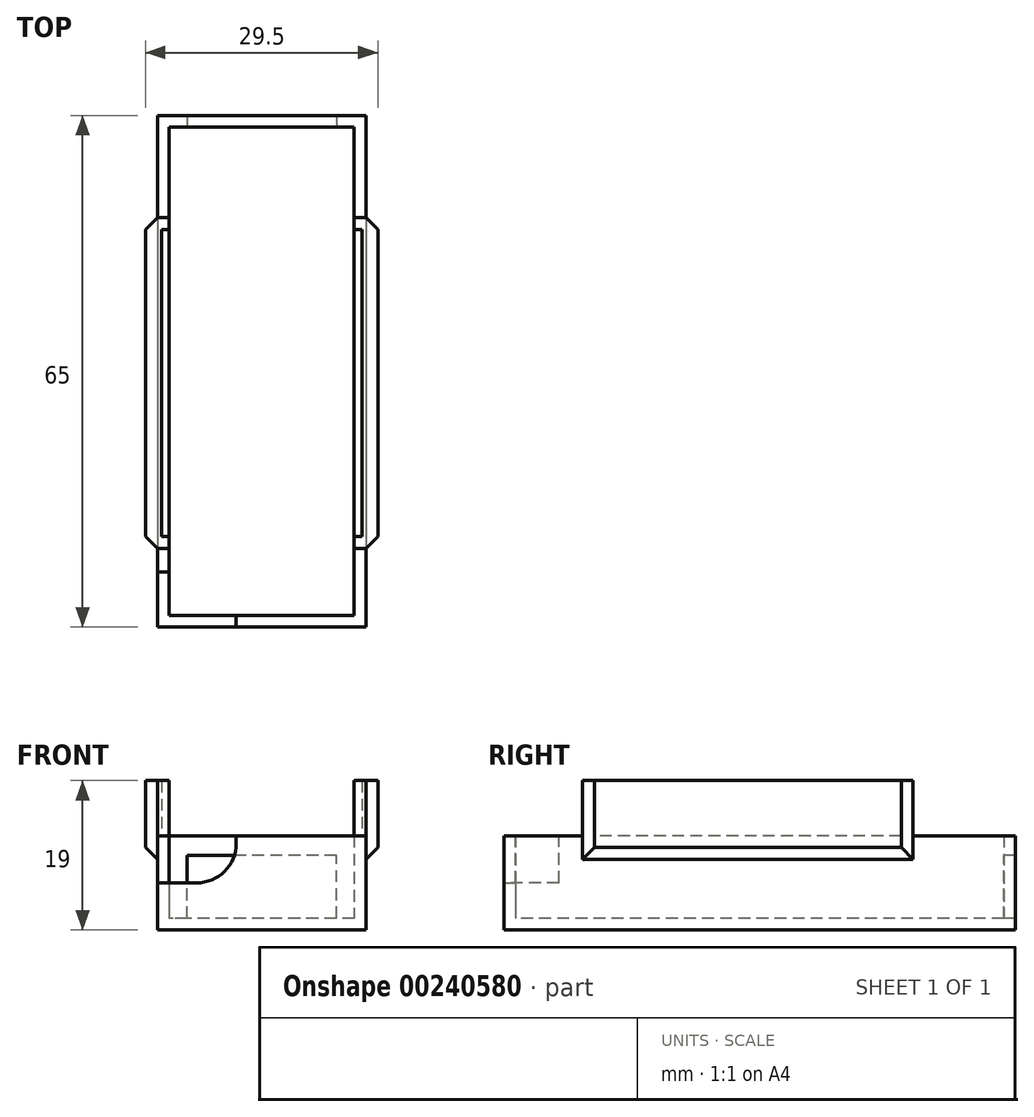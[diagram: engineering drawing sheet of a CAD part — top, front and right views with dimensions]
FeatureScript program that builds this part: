
annotation { "Feature Type Name" : "Feature", "Feature Type Description" : "" }
export const myFeature = defineFeature(function(context is Context, id is Id, definition is map)
    precondition{}
    {
        {
            var Q0;
            Q0=qCreatedBy(makeId("Top.planeOp"),FACE);
            var sketch = newSketch(context, id + "F0", { "sketchPlane" : qUnion([Q0])});
            skLineSegment(sketch, "E0.bottom", {"start": v(11.75, 31) * mm, "end": v(-11.75, 31) * mm});
            skLineSegment(sketch, "E0.top", {"start": v(11.75, -31) * mm, "end": v(-11.75, -31) * mm});
            skLineSegment(sketch, "E0.left", {"start": v(11.75, 31) * mm, "end": v(11.75, -31) * mm});
            skLineSegment(sketch, "E0.right", {"start": v(-11.75, 31) * mm, "end": v(-11.75, -31) * mm});
            skPoint(sketch, "E0.middle", {"position": v(0, 0) * mm});
            skSolve(sketch);
        }
        {
            var Q0;
            Q0=makeQuery(id+"F0.imprint","IMPRINT",FACE,{"disambiguationData":[TD([[makeQuery(id+"F0.imprint","IMPRINT",EDGE,{"derivedFrom":sQuery(id+"F0.wireOp",EDGE,"E0.bottom")}),1.0]])]});
            extrude(context, id + "F1", {"entities" : qUnion([Q0]), "depth" : 1.5 * mm});
        }
        {
            var Q0;
            Q0=qCreatedBy(makeId("Top.planeOp"),FACE);
            var sketch = newSketch(context, id + "F2", { "sketchPlane" : qUnion([Q0])});
            skLineSegment(sketch, "E1.0", {"start": v(11.75, -31) * mm, "end": v(-11.75, -31) * mm});
            skLineSegment(sketch, "E1.1", {"start": v(-11.75, 31) * mm, "end": v(-11.75, -31) * mm});
            skLineSegment(sketch, "E1.2", {"start": v(11.75, 31) * mm, "end": v(11.75, -31) * mm});
            skLineSegment(sketch, "E1.3", {"start": v(11.75, 31) * mm, "end": v(-11.75, 31) * mm});
            skLineSegment(sketch, "E2.0", {"start": v(13.25, -32.5) * mm, "end": v(-13.25, -32.5) * mm});
            skLineSegment(sketch, "E2.1", {"start": v(13.25, 32.5) * mm, "end": v(13.25, -32.5) * mm});
            skLineSegment(sketch, "E2.2", {"start": v(13.25, 32.5) * mm, "end": v(-13.25, 32.5) * mm});
            skLineSegment(sketch, "E2.3", {"start": v(-13.25, 32.5) * mm, "end": v(-13.25, -32.5) * mm});
            skSolve(sketch);
        }
        {
            var Q0;
            Q0=makeQuery(id+"F2.imprint","IMPRINT",FACE,{"disambiguationData":[TD([[makeQuery(id+"F2.imprint","IMPRINT",EDGE,{"derivedFrom":sQuery(id+"F2.wireOp",EDGE,"E1.0")}),1.0]])]});
            extrude(context, id + "F3", {"entities" : qUnion([Q0]), "operationType" : NewBodyOperationType.ADD, "depth" : 12 * mm});
        }
        {
            var Q0;
            Q0=makeQuery(id+"F3.opExtrude","CAP_FACE",FACE,{"disambiguationData":[OSD([sQuery(id+"F2.wireOp",EDGE,"E1.0"),sQuery(id+"F2.wireOp",EDGE,"E1.1"),sQuery(id+"F2.wireOp",EDGE,"E1.2"),sQuery(id+"F2.wireOp",EDGE,"E1.3"),sQuery(id+"F2.wireOp",EDGE,"E2.0"),sQuery(id+"F2.wireOp",EDGE,"E2.1"),sQuery(id+"F2.wireOp",EDGE,"E2.2"),sQuery(id+"F2.wireOp",EDGE,"E2.3")])],"isStart":false});
            var sketch = newSketch(context, id + "F4", { "sketchPlane" : qUnion([Q0])});
            skLineSegment(sketch, "E3.bottom", {"start": v(12.75, -21) * mm, "end": v(-12.75, -21) * mm, "construction": true});
            skLineSegment(sketch, "E3.top", {"start": v(12.75, 18) * mm, "end": v(-12.75, 18) * mm, "construction": true});
            skLineSegment(sketch, "E3.left", {"start": v(12.75, -21) * mm, "end": v(12.75, 18) * mm, "construction": true});
            skLineSegment(sketch, "E3.right", {"start": v(-12.75, -21) * mm, "end": v(-12.75, 18) * mm, "construction": true});
            skPoint(sketch, "E4", {"position": v(0, -21) * mm});
            skLineSegment(sketch, "E5.bottom", {"start": v(-12.75, -21) * mm, "end": v(-14.75, -21) * mm});
            skLineSegment(sketch, "E5.top", {"start": v(-12.75, 18) * mm, "end": v(-14.75, 18) * mm});
            skLineSegment(sketch, "E5.left", {"start": v(-12.75, -21) * mm, "end": v(-12.75, 18) * mm});
            skLineSegment(sketch, "E5.right", {"start": v(-14.75, -21) * mm, "end": v(-14.75, 18) * mm});
            skLineSegment(sketch, "E6.bottom", {"start": v(12.75, -21) * mm, "end": v(14.75, -21) * mm});
            skLineSegment(sketch, "E6.top", {"start": v(12.75, 18) * mm, "end": v(14.75, 18) * mm});
            skLineSegment(sketch, "E6.left", {"start": v(12.75, -21) * mm, "end": v(12.75, 18) * mm});
            skLineSegment(sketch, "E6.right", {"start": v(14.75, -21) * mm, "end": v(14.75, 18) * mm});
            skSolve(sketch);
        }
        {
            var Q0;
            Q0 = qSketchRegion(id + "F4", true);
            extrude(context, id + "F5", {"entities" : qUnion([Q0]), "operationType" : NewBodyOperationType.ADD, "depth" : 7 * mm});
        }
        {
            var Q0;
            Q0=makeQuery(id+"F3.opExtrude","CAP_FACE",FACE,{"disambiguationData":[OSD([sQuery(id+"F2.wireOp",EDGE,"E1.0"),sQuery(id+"F2.wireOp",EDGE,"E1.1"),sQuery(id+"F2.wireOp",EDGE,"E1.2"),sQuery(id+"F2.wireOp",EDGE,"E1.3"),sQuery(id+"F2.wireOp",EDGE,"E2.0"),sQuery(id+"F2.wireOp",EDGE,"E2.1"),sQuery(id+"F2.wireOp",EDGE,"E2.2"),sQuery(id+"F2.wireOp",EDGE,"E2.3")])],"isStart":false});
            var sketch = newSketch(context, id + "F6", { "sketchPlane" : qUnion([Q0])});
            skLineSegment(sketch, "E7.bottom", {"start": v(11.75, -21) * mm, "end": v(14.75, -21) * mm});
            skLineSegment(sketch, "E7.top", {"start": v(11.75, -22.5) * mm, "end": v(13.25, -22.5) * mm});
            skLineSegment(sketch, "E7.left", {"start": v(11.75, -21) * mm, "end": v(11.75, -22.5) * mm});
            skLineSegment(sketch, "E7.right", {"start": v(14.75, -21) * mm, "end": v(13.25, -22.5) * mm});
            skPoint(sketch, "E8.0", {"position": v(14.75, -21) * mm});
            skPoint(sketch, "E9.0", {"position": v(14.75, -1.5) * mm});
            skLineSegment(sketch, "E10", {"start": v(14.75, -1.5) * mm, "end": v(21.45, -1.5) * mm, "construction": true});
            skLineSegment(sketch, "E11.MirrorCS", {"start": v(11.75, 18) * mm, "end": v(14.75, 18) * mm});
            skLineSegment(sketch, "E12.MirrorCS", {"start": v(11.75, 19.5) * mm, "end": v(13.25, 19.5) * mm});
            skLineSegment(sketch, "E13.MirrorCS", {"start": v(11.75, 18) * mm, "end": v(11.75, 19.5) * mm});
            skLineSegment(sketch, "E14.MirrorCS", {"start": v(14.75, 18) * mm, "end": v(13.25, 19.5) * mm});
            skPoint(sketch, "E15.MirrorP", {"position": v(14.75, 18) * mm});
            skLineSegment(sketch, "E16", {"start": v(0, 1.04) * mm, "end": v(0, -9.48) * mm, "construction": true});
            skPoint(sketch, "E17.MirrorP", {"position": v(-14.75, 18) * mm});
            skLineSegment(sketch, "E18.MirrorCS", {"start": v(-14.75, 18) * mm, "end": v(-13.25, 19.5) * mm});
            skLineSegment(sketch, "E19.MirrorCS", {"start": v(-11.75, 18) * mm, "end": v(-14.75, 18) * mm});
            skLineSegment(sketch, "E20.MirrorCS", {"start": v(-11.75, 19.5) * mm, "end": v(-13.25, 19.5) * mm});
            skLineSegment(sketch, "E21.MirrorCS", {"start": v(-11.75, 18) * mm, "end": v(-11.75, 19.5) * mm});
            skLineSegment(sketch, "E22.MirrorCS", {"start": v(-11.75, -21) * mm, "end": v(-11.75, -22.5) * mm});
            skLineSegment(sketch, "E23.MirrorCS", {"start": v(-11.75, -22.5) * mm, "end": v(-13.25, -22.5) * mm});
            skLineSegment(sketch, "E24.MirrorCS", {"start": v(-14.75, -21) * mm, "end": v(-13.25, -22.5) * mm});
            skLineSegment(sketch, "E25.MirrorCS", {"start": v(-11.75, -21) * mm, "end": v(-14.75, -21) * mm});
            skPoint(sketch, "E26.MirrorP", {"position": v(-14.75, -21) * mm});
            skSolve(sketch);
        }
        {
            var Q0;
            Q0 = qSketchRegion(id + "F6", true);
            var Q1;
            Q1=makeQuery(id+"F5.opExtrude","CAP_FACE",FACE,{"disambiguationData":[OSD([sQuery(id+"F4.wireOp",EDGE,"E6.bottom"),sQuery(id+"F4.wireOp",EDGE,"E6.top"),sQuery(id+"F4.wireOp",EDGE,"E6.left"),sQuery(id+"F4.wireOp",EDGE,"E6.right")])],"isStart":false});
            extrude(context, id + "F7", {"entities" : qUnion([Q0]), "operationType" : NewBodyOperationType.ADD, "endBound" : BoundingType.UP_TO_SURFACE, "endBoundEntityFace" : qUnion([Q1]), "depth" : 25 * mm});
        }
        {
            var Q0;
            Q0=makeQuery(id+"F1.opExtrude","CAP_FACE",FACE,{"disambiguationData":[OSD([sQuery(id+"F0.wireOp",EDGE,"E0.bottom"),sQuery(id+"F0.wireOp",EDGE,"E0.top"),sQuery(id+"F0.wireOp",EDGE,"E0.left"),sQuery(id+"F0.wireOp",EDGE,"E0.right")])],"isStart":false});
            var sketch = newSketch(context, id + "F8", { "sketchPlane" : qUnion([Q0])});
            skLineSegment(sketch, "E27.bottom", {"start": v(-9.5, 33.5) * mm, "end": v(9.5, 33.5) * mm});
            skLineSegment(sketch, "E27.top", {"start": v(-9.5, 28.5) * mm, "end": v(9.5, 28.5) * mm});
            skLineSegment(sketch, "E27.left", {"start": v(-9.5, 33.5) * mm, "end": v(-9.5, 28.5) * mm});
            skLineSegment(sketch, "E27.right", {"start": v(9.5, 33.5) * mm, "end": v(9.5, 28.5) * mm});
            skPoint(sketch, "E27.middle", {"position": v(0, 31) * mm});
            skSolve(sketch);
        }
        {
            var Q0;
            Q0 = qSketchRegion(id + "F8", true);
            extrude(context, id + "F9", {"entities" : qUnion([Q0]), "operationType" : NewBodyOperationType.REMOVE, "depth" : 8 * mm});
        }
        {
            var Q0;
            {var subQ3=sQuery(id+"F2.wireOp",EDGE,"E2.3");var subQ4=sQuery(id+"F2.wireOp",EDGE,"E2.1");var subQ5=sQuery(id+"F2.wireOp",EDGE,"E1.0");var subQ6=sQuery(id+"F2.wireOp",EDGE,"E1.1");var subQ7=sQuery(id+"F2.wireOp",EDGE,"E1.2");var subQ10=sQuery(id+"F2.wireOp",EDGE,"E2.0");Q0=makeQuery(id+"F7.boolean.opBoolean","SPLIT",FACE,{"disambiguationData":[TD([makeQuery(id+"F3.opExtrude","SWEPT_FACE",FACE,{"disambiguationData":[OSD([subQ5])]})])],"derivedFrom":makeQuery(id+"F3.opExtrude","CAP_FACE",FACE,{"disambiguationData":[OSD([subQ5,subQ6,subQ7,sQuery(id+"F2.wireOp",EDGE,"E1.3"),subQ10,subQ4,sQuery(id+"F2.wireOp",EDGE,"E2.2"),subQ3])],"isStart":false})});}
            var sketch = newSketch(context, id + "F10", { "sketchPlane" : qUnion([Q0])});
            skLineSegment(sketch, "E28.bottom", {"start": v(-13.25, -32.5) * mm, "end": v(-3.25, -32.5) * mm});
            skLineSegment(sketch, "E28.top", {"start": v(-13.25, -25.5) * mm, "end": v(-3.25, -25.5) * mm});
            skLineSegment(sketch, "E28.left", {"start": v(-13.25, -32.5) * mm, "end": v(-13.25, -25.5) * mm});
            skLineSegment(sketch, "E28.right", {"start": v(-3.25, -32.5) * mm, "end": v(-3.25, -25.5) * mm});
            skSolve(sketch);
        }
        {
            var Q0;
            {var subQ14=sQuery(id+"F10.wireOp",EDGE,"E28.bottom");Q0=makeQuery(id+"F10.imprint","IMPRINT",FACE,{"disambiguationData":[TD([[makeQuery(id+"F10.imprint","IMPRINT",EDGE,{"derivedFrom":subQ14}),-1.0]])]});}
            extrude(context, id + "F11", {"entities" : qUnion([Q0]), "operationType" : NewBodyOperationType.REMOVE, "oppositeDirection" : true, "depth" : 6 * mm});
        }
        {
            var Q0;
            Q0=makeQuery(id+"F11.boolean.opBoolean","COPY",EDGE,{"derivedFrom":makeQuery(id+"F11.opExtrude","CAP_EDGE",EDGE,{"disambiguationData":[OSD([sQuery(id+"F10.wireOp",EDGE,"E28.right")])],"isStart":false})});
            fillet(context, id + "F12", {"entities" : qUnion([Q0]), "radius" : 5 * mm, "tangentPropagation" : true, "allowEdgeOverflow" : false});
        }
        {
            var Q0;
            Q0=makeQuery(id+"F7.opExtrude","CAP_FACE",FACE,{"disambiguationData":[OSD([sQuery(id+"F6.wireOp",EDGE,"E22.MirrorCS"),sQuery(id+"F6.wireOp",EDGE,"E23.MirrorCS"),sQuery(id+"F6.wireOp",EDGE,"E24.MirrorCS"),sQuery(id+"F6.wireOp",EDGE,"E25.MirrorCS")])],"isStart":true});
            var Q1;
            Q1=makeQuery(id+"F7.boolean.opBoolean","MERGE",FACE,{"derivedFrom":[makeQuery(id+"F5.opExtrude","CAP_FACE",FACE,{"disambiguationData":[OSD([sQuery(id+"F4.wireOp",EDGE,"E6.bottom"),sQuery(id+"F4.wireOp",EDGE,"E6.top"),sQuery(id+"F4.wireOp",EDGE,"E6.left"),sQuery(id+"F4.wireOp",EDGE,"E6.right")])],"isStart":true}),makeQuery(id+"F7.opExtrude","CAP_FACE",FACE,{"disambiguationData":[OSD([sQuery(id+"F6.wireOp",EDGE,"E7.bottom"),sQuery(id+"F6.wireOp",EDGE,"E7.top"),sQuery(id+"F6.wireOp",EDGE,"E7.left"),sQuery(id+"F6.wireOp",EDGE,"E7.right")])],"isStart":true}),makeQuery(id+"F7.opExtrude","CAP_FACE",FACE,{"disambiguationData":[OSD([sQuery(id+"F6.wireOp",EDGE,"E11.MirrorCS"),sQuery(id+"F6.wireOp",EDGE,"E12.MirrorCS"),sQuery(id+"F6.wireOp",EDGE,"E13.MirrorCS"),sQuery(id+"F6.wireOp",EDGE,"E14.MirrorCS")])],"isStart":true})]});
            extrude(context, id + "F13", {"entities" : qUnion([Q0, Q1]), "operationType" : NewBodyOperationType.ADD, "depth" : 3 * mm});
        }
        {
            var Q0;
            Q0=makeQuery(id+"F13.opExtrude","CAP_EDGE",EDGE,{"disambiguationData":[OSD([sQuery(id+"F4.wireOp",EDGE,"E5.right")])],"isStart":false});
            var Q1;
            Q1=makeQuery(id+"F13.opExtrude","CAP_EDGE",EDGE,{"disambiguationData":[OSD([sQuery(id+"F4.wireOp",EDGE,"E6.right")])],"isStart":false});
            chamfer(context, id + "F14", {"entities" : qUnion([Q0, Q1]), "width" : 1.5 * mm, "tangentPropagation" : true});
        }
    });
